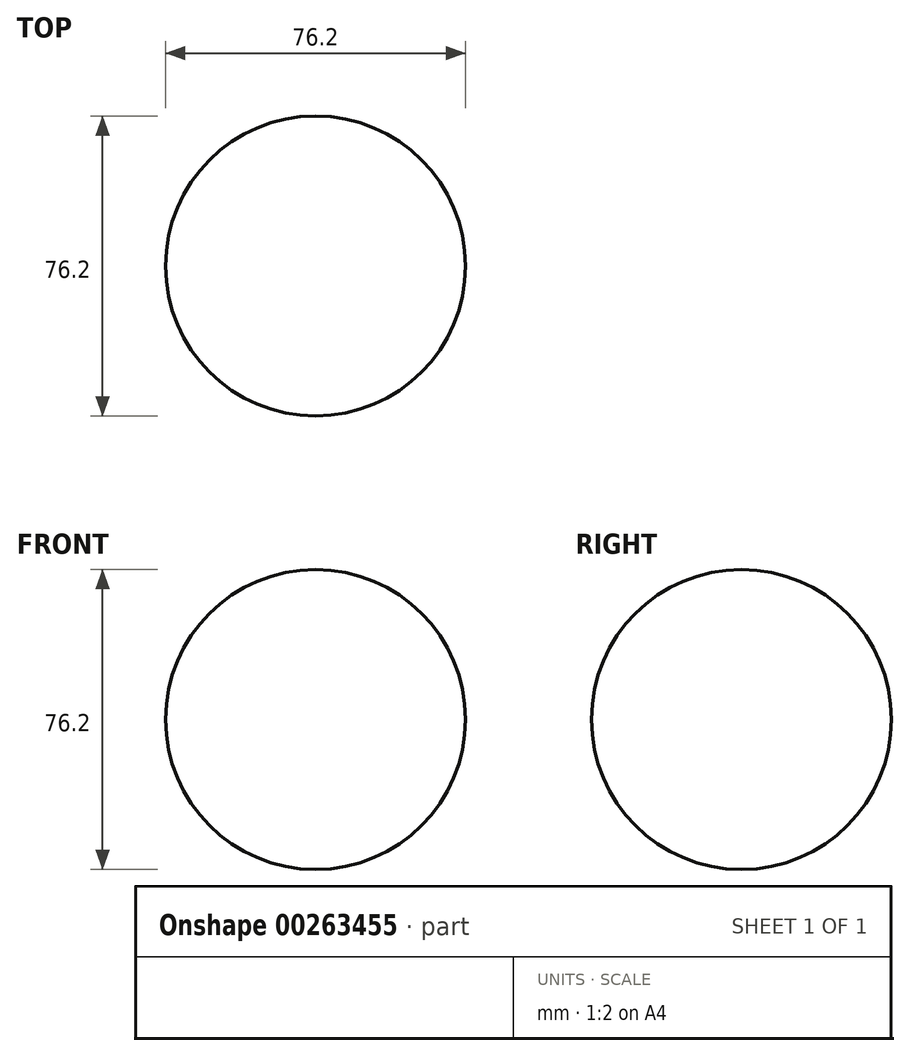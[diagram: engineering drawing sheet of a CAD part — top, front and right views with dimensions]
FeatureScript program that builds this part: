
annotation { "Feature Type Name" : "Feature", "Feature Type Description" : "" }
export const myFeature = defineFeature(function(context is Context, id is Id, definition is map)
    precondition{}
    {
        {
            var Q0;
            Q0=qCreatedBy(makeId("Front.planeOp"),FACE);
            var sketch = newSketch(context, id + "F0", { "sketchPlane" : qUnion([Q0])});
            skArc(sketch, "E0", {"start": v(0, 38.1) * mm, "mid": v(-38.1, 0) * mm, "end": v(0, -38.1) * mm});
            skLineSegment(sketch, "E1", {"start": v(0, 57.79) * mm, "end": v(0, -68.45) * mm, "construction": true});
            skSolve(sketch);
        }
        {
            var Q0;
            Q0=sQuery(id+"F0.wireOp",EDGE,"E0");
            var Q1;
            Q1=sQuery(id+"F0.wireOp",EDGE,"E1");
            revolve(context, id + "F1", {"bodyType" : ToolBodyType.SURFACE, "surfaceEntities" : qUnion([Q0]), "axis" : qUnion([Q1]), "revolveType" : RevolveType.FULL});
        }
    });
